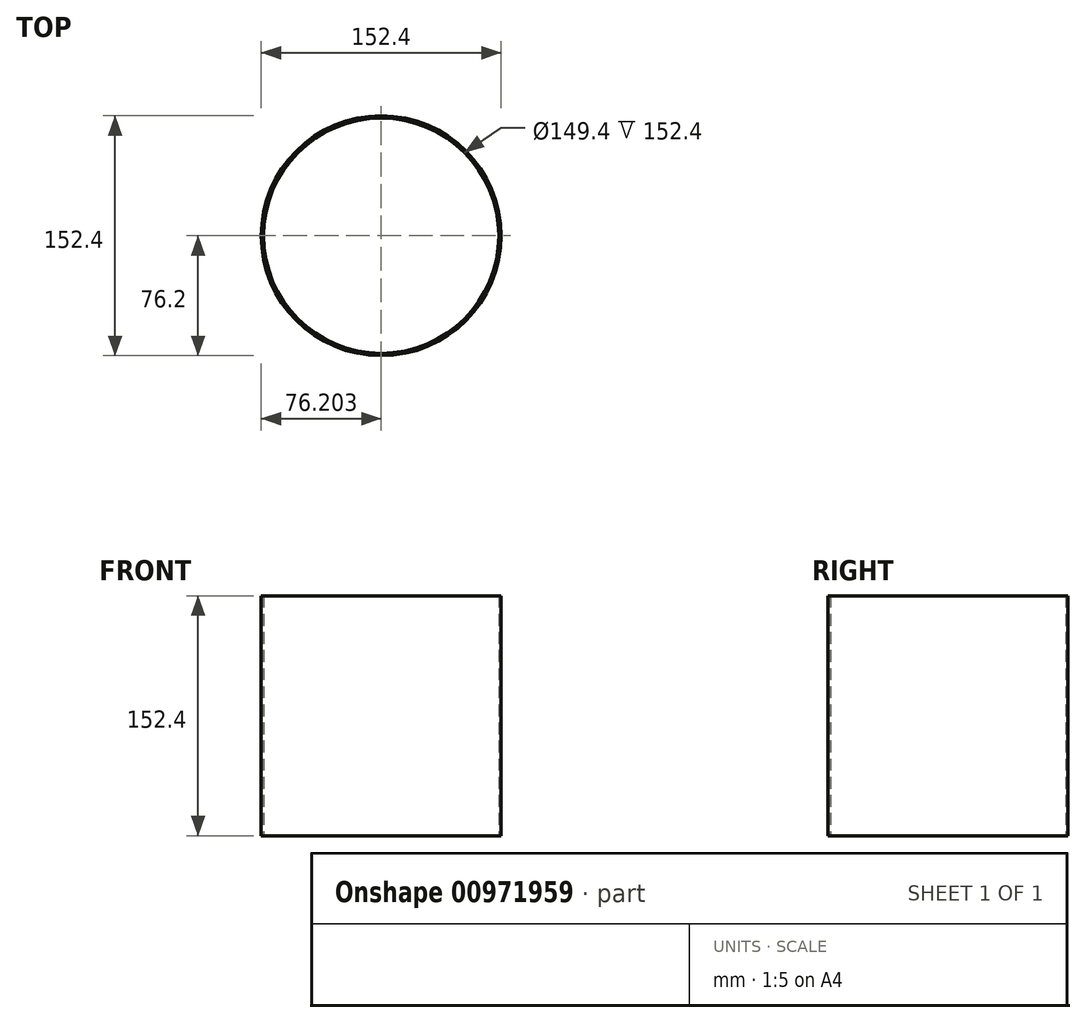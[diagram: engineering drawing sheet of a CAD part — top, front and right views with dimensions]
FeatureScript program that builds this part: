
annotation { "Feature Type Name" : "Feature", "Feature Type Description" : "" }
export const myFeature = defineFeature(function(context is Context, id is Id, definition is map)
    precondition{}
    {
        {
            var Q0;
            Q0=qCreatedBy(makeId("Front.planeOp"),FACE);
            var sketch = newSketch(context, id + "F0", { "sketchPlane" : qUnion([Q0])});
            skLineSegment(sketch, "E0.bottom", {"start": v(43.07, -81.5) * mm, "end": v(-33.13, -81.5) * mm});
            skLineSegment(sketch, "E0.top", {"start": v(43.07, 70.9) * mm, "end": v(-33.13, 70.9) * mm});
            skLineSegment(sketch, "E0.left", {"start": v(43.07, -81.5) * mm, "end": v(43.07, 70.9) * mm});
            skLineSegment(sketch, "E0.right", {"start": v(-33.13, -81.5) * mm, "end": v(-33.13, 70.9) * mm});
            skSolve(sketch);
        }
        {
            var Q0;
            Q0=makeQuery(id+"F0.imprint","IMPRINT",FACE,{"disambiguationData":[TD([[makeQuery(id+"F0.imprint","IMPRINT",EDGE,{"derivedFrom":sQuery(id+"F0.wireOp",EDGE,"E0.bottom")}),-1.0]])]});
            var Q1;
            Q1=sQuery(id+"F0.wireOp",EDGE,"E0.left");
            revolve(context, id + "F1", {"surfaceOperationType" : NewSurfaceOperationType.NEW, "entities" : qUnion([Q0]), "axis" : qUnion([Q1]), "revolveType" : RevolveType.FULL});
        }
        {
            var Q0;
            Q0=makeQuery(id+"F1.opRevolve","SWEPT_FACE",FACE,{"disambiguationData":[OSD([sQuery(id+"F0.wireOp",EDGE,"E0.bottom")])]});
            var sketch = newSketch(context, id + "F2", { "sketchPlane" : qUnion([Q0])});
            skCircle(sketch, "E1.0", {"center": v(43.07, 0) * mm, "radius": 74.7 * mm});
            skSolve(sketch);
        }
        {
            var Q0;
            Q0=makeQuery(id+"F2.imprint","IMPRINT",FACE,{"disambiguationData":[TD([[makeQuery(id+"F2.imprint","IMPRINT",EDGE,{"derivedFrom":sQuery(id+"F2.wireOp",EDGE,"E1.0")}),1.0]])]});
            extrude(context, id + "F3", {"entities" : qUnion([Q0]), "operationType" : NewBodyOperationType.REMOVE, "oppositeDirection" : true, "depth" : 207 * mm, "offsetDistance" : 25.4 * mm});
        }
    });
